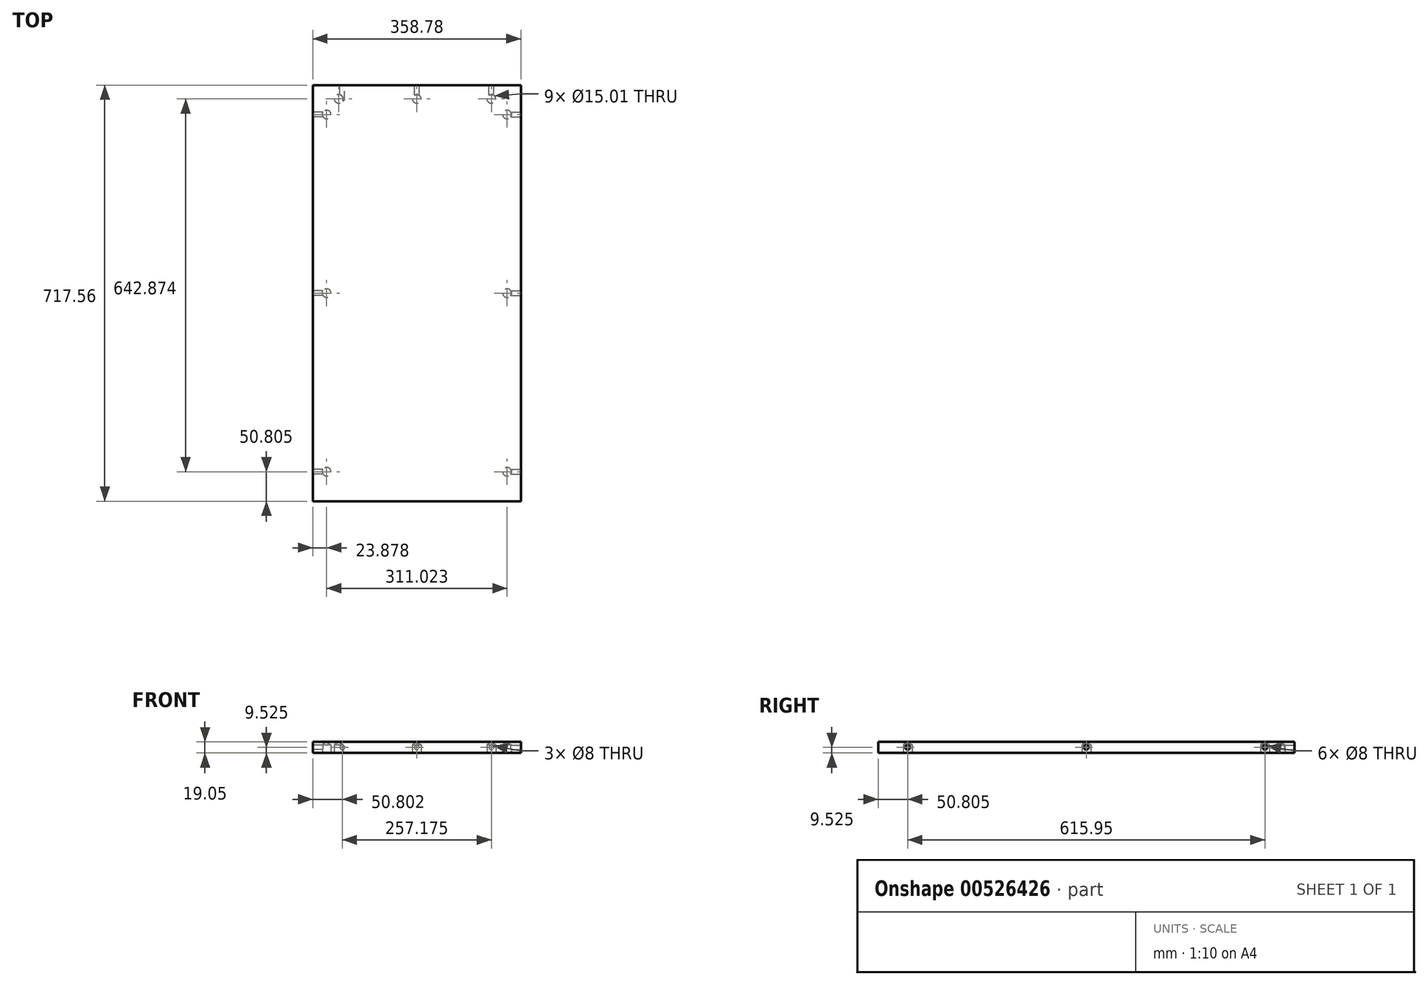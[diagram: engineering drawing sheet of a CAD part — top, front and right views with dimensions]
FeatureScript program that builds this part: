
annotation { "Feature Type Name" : "Feature", "Feature Type Description" : "" }
export const myFeature = defineFeature(function(context is Context, id is Id, definition is map)
    precondition{}
    {
        {
            var Q0;
            Q0=qCreatedBy(makeId("Top.planeOp"),FACE);
            var sketch = newSketch(context, id + "F0", { "sketchPlane" : qUnion([Q0])});
            skLineSegment(sketch, "E0.bottom", {"start": v(179.39, 358.78) * mm, "end": v(-179.39, 358.78) * mm});
            skLineSegment(sketch, "E0.top", {"start": v(179.39, -358.78) * mm, "end": v(-179.39, -358.78) * mm});
            skLineSegment(sketch, "E0.left", {"start": v(179.39, 358.77) * mm, "end": v(179.39, -358.78) * mm});
            skLineSegment(sketch, "E0.right", {"start": v(-179.39, 358.77) * mm, "end": v(-179.39, -358.78) * mm});
            skPoint(sketch, "E0.middle", {"position": v(0, 0) * mm});
            skSolve(sketch);
        }
        {
            var Q0;
            Q0=makeQuery(id+"F0.imprint","IMPRINT",FACE,{"disambiguationData":[TD([[makeQuery(id+"F0.imprint","IMPRINT",EDGE,{"derivedFrom":sQuery(id+"F0.wireOp",EDGE,"E0.bottom")}),1.0]])]});
            extrude(context, id + "F1", {"entities" : qUnion([Q0]), "depth" : 19.05 * mm, "offsetDistance" : 25.4 * mm});
        }
        {
            var Q0;
            Q0=makeQuery(id+"F1.opExtrude","SWEPT_FACE",FACE,{"disambiguationData":[OSD([sQuery(id+"F0.wireOp",EDGE,"E0.left")])]});
            var sketch = newSketch(context, id + "F2", { "sketchPlane" : qUnion([Q0])});
            skPoint(sketch, "E1", {"position": v(-307.98, 9.53) * mm});
            skPoint(sketch, "E2", {"position": v(0, 9.53) * mm});
            skPoint(sketch, "E3", {"position": v(307.97, 9.53) * mm});
            skSolve(sketch);
        }
        {
            var Q0;
            Q0=sQuery(id+"F2.wireOp",VERTEX,"E1");
            var Q1;
            Q1=sQuery(id+"F2.wireOp",VERTEX,"E2");
            var Q2;
            Q2=sQuery(id+"F2.wireOp",VERTEX,"E3");
            var Q3;
            Q3=makeQuery(id+"F1.opExtrude","SWEPT_BODY",BODY,{"disambiguationData":[OSD([sQuery(id+"F0.wireOp",EDGE,"E0.bottom"),sQuery(id+"F0.wireOp",EDGE,"E0.top"),sQuery(id+"F0.wireOp",EDGE,"E0.left"),sQuery(id+"F0.wireOp",EDGE,"E0.right")])]});
            hole(context, id + "F3", {"style" : HoleStyle.SIMPLE, "endStyle" : HoleEndStyle.BLIND, "holeDiameter" : 8 * mm, "holeDepth" : 25.4 * mm, "isTappedThrough" : true, "tappedDepth" : 12.7 * mm, "tapClearance" : 3, "startFromSketch" : true, "locations" : qUnion([Q0, Q1, Q2]), "scope" : qUnion([Q3])});
        }
        {
            var Q0;
            Q0=makeQuery(id+"F1.opExtrude","SWEPT_FACE",FACE,{"disambiguationData":[OSD([sQuery(id+"F0.wireOp",EDGE,"E0.right")])]});
            var sketch = newSketch(context, id + "F4", { "sketchPlane" : qUnion([Q0])});
            skPoint(sketch, "E4", {"position": v(0, 9.53) * mm});
            skPoint(sketch, "E5", {"position": v(307.98, 9.53) * mm});
            skPoint(sketch, "E6", {"position": v(-307.98, 9.53) * mm});
            skSolve(sketch);
        }
        {
            var Q0;
            Q0=sQuery(id+"F4.wireOp",VERTEX,"E6");
            var Q1;
            Q1=sQuery(id+"F4.wireOp",VERTEX,"E4");
            var Q2;
            Q2=sQuery(id+"F4.wireOp",VERTEX,"E5");
            var Q3;
            Q3=makeQuery(id+"F1.opExtrude","SWEPT_BODY",BODY,{"disambiguationData":[OSD([sQuery(id+"F0.wireOp",EDGE,"E0.bottom"),sQuery(id+"F0.wireOp",EDGE,"E0.top"),sQuery(id+"F0.wireOp",EDGE,"E0.left"),sQuery(id+"F0.wireOp",EDGE,"E0.right")])]});
            hole(context, id + "F5", {"style" : HoleStyle.SIMPLE, "endStyle" : HoleEndStyle.BLIND, "holeDiameter" : 8 * mm, "holeDepth" : 25.4 * mm, "isTappedThrough" : true, "tappedDepth" : 12.7 * mm, "tapClearance" : 3, "startFromSketch" : true, "locations" : qUnion([Q0, Q1, Q2]), "scope" : qUnion([Q3])});
        }
        {
            var Q0;
            Q0=makeQuery(id+"F1.opExtrude","SWEPT_FACE",FACE,{"disambiguationData":[OSD([sQuery(id+"F0.wireOp",EDGE,"E0.bottom")])]});
            var sketch = newSketch(context, id + "F6", { "sketchPlane" : qUnion([Q0])});
            skPoint(sketch, "E7", {"position": v(-128.59, 9.53) * mm});
            skPoint(sketch, "E8", {"position": v(0, 9.53) * mm});
            skPoint(sketch, "E9", {"position": v(128.59, 9.53) * mm});
            skSolve(sketch);
        }
        {
            var Q0;
            Q0=sQuery(id+"F6.wireOp",VERTEX,"E7");
            var Q1;
            Q1=sQuery(id+"F6.wireOp",VERTEX,"E8");
            var Q2;
            Q2=sQuery(id+"F6.wireOp",VERTEX,"E9");
            var Q3;
            Q3=makeQuery(id+"F1.opExtrude","SWEPT_BODY",BODY,{"disambiguationData":[OSD([sQuery(id+"F0.wireOp",EDGE,"E0.bottom"),sQuery(id+"F0.wireOp",EDGE,"E0.top"),sQuery(id+"F0.wireOp",EDGE,"E0.left"),sQuery(id+"F0.wireOp",EDGE,"E0.right")])]});
            hole(context, id + "F7", {"style" : HoleStyle.SIMPLE, "endStyle" : HoleEndStyle.BLIND, "holeDiameter" : 8 * mm, "holeDepth" : 25.4 * mm, "isTappedThrough" : true, "tappedDepth" : 12.7 * mm, "tapClearance" : 3, "startFromSketch" : true, "locations" : qUnion([Q0, Q1, Q2]), "scope" : qUnion([Q3])});
        }
        {
            var Q0;
            Q0=makeQuery(id+"F1.opExtrude","CAP_FACE",FACE,{"disambiguationData":[OSD([sQuery(id+"F0.wireOp",EDGE,"E0.bottom"),sQuery(id+"F0.wireOp",EDGE,"E0.top"),sQuery(id+"F0.wireOp",EDGE,"E0.left"),sQuery(id+"F0.wireOp",EDGE,"E0.right")])],"isStart":true});
            var sketch = newSketch(context, id + "F8", { "sketchPlane" : qUnion([Q0])});
            skLineSegment(sketch, "E10", {"start": v(-179.39, 358.78) * mm, "end": v(-155.51, 358.78) * mm});
            skPoint(sketch, "E11", {"position": v(-134.62, -334.9) * mm});
            skPoint(sketch, "E12", {"position": v(0, -334.9) * mm});
            skPoint(sketch, "E13", {"position": v(128.59, -334.9) * mm});
            skPoint(sketch, "E14", {"position": v(155.51, -307.98) * mm});
            skPoint(sketch, "E15", {"position": v(-155.51, -307.98) * mm});
            skPoint(sketch, "E16", {"position": v(-155.51, 307.97) * mm});
            skPoint(sketch, "E17", {"position": v(155.51, 307.97) * mm});
            skPoint(sketch, "E18", {"position": v(155.51, 0) * mm});
            skPoint(sketch, "E19", {"position": v(-155.51, 0) * mm});
            skSolve(sketch);
        }
        {
            var Q0;
            Q0=sQuery(id+"F8.wireOp",VERTEX,"E16");
            var Q1;
            Q1=sQuery(id+"F8.wireOp",VERTEX,"E17");
            var Q2;
            Q2=sQuery(id+"F8.wireOp",VERTEX,"E18");
            var Q3;
            Q3=sQuery(id+"F8.wireOp",VERTEX,"E19");
            var Q4;
            Q4=sQuery(id+"F8.wireOp",VERTEX,"E15");
            var Q5;
            Q5=sQuery(id+"F8.wireOp",VERTEX,"E11");
            var Q6;
            Q6=sQuery(id+"F8.wireOp",VERTEX,"E12");
            var Q7;
            Q7=sQuery(id+"F8.wireOp",VERTEX,"E13");
            var Q8;
            Q8=sQuery(id+"F8.wireOp",VERTEX,"E14");
            var Q9;
            Q9=makeQuery(id+"F1.opExtrude","SWEPT_BODY",BODY,{"disambiguationData":[OSD([sQuery(id+"F0.wireOp",EDGE,"E0.bottom"),sQuery(id+"F0.wireOp",EDGE,"E0.top"),sQuery(id+"F0.wireOp",EDGE,"E0.left"),sQuery(id+"F0.wireOp",EDGE,"E0.right")])]});
            hole(context, id + "F9", {"style" : HoleStyle.SIMPLE, "endStyle" : HoleEndStyle.BLIND, "holeDiameter" : 15 * mm, "holeDepth" : 14.22 * mm, "isTappedThrough" : true, "tappedDepth" : 12.7 * mm, "tapClearance" : 3, "startFromSketch" : true, "locations" : qUnion([Q0, Q1, Q2, Q3, Q4, Q5, Q6, Q7, Q8]), "scope" : qUnion([Q9])});
        }
    });
